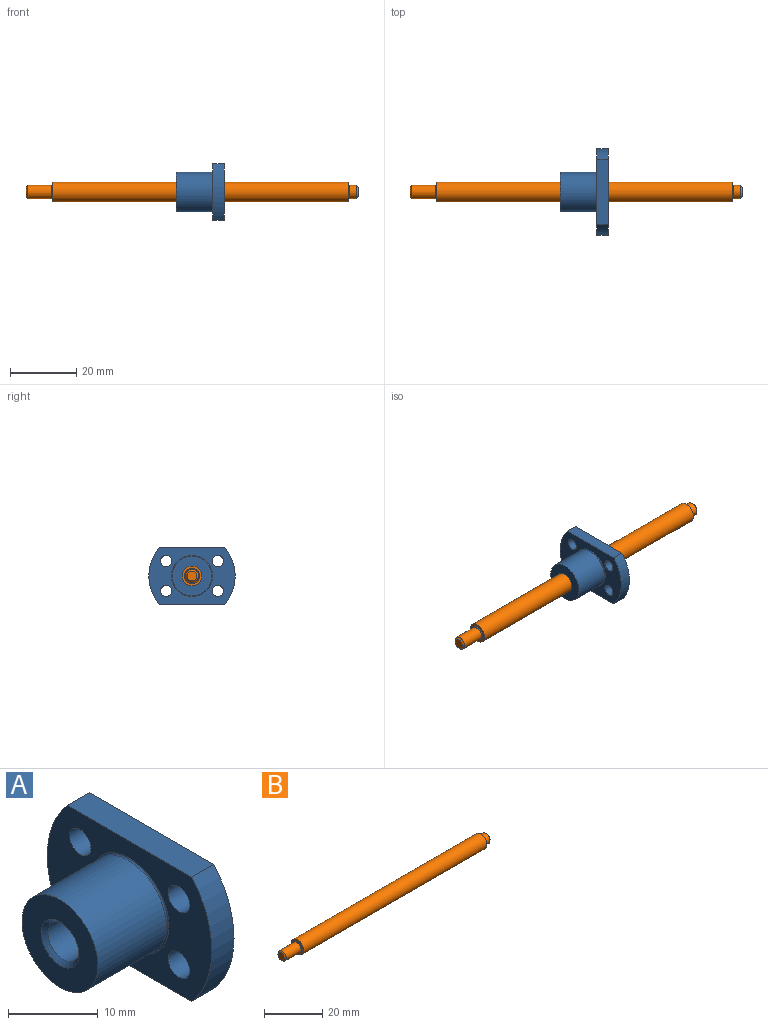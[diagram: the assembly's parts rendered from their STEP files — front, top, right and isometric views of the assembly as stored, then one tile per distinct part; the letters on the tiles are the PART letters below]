
ASSEMBLY  parts=2 mates=1
PART A: 16 faces, bbox 14.5x26x17 mm
  f0: plane 12x12mm, normal (-1,0,0), area 84.8mm2, adj f5,f7
  f1: plane 26x17mm, normal (1,0,0), area 343.5mm2, adj f2,f3,f6,f9,f10,f11,f12,f13
  f2: plane 19.67x3.5mm, normal (0,0,1), area 68.9mm2, adj f1,f3,f8,f14
  f3: cylinder r=13mm len=17mm, axis (1,0,0), area 64.9mm2, adj f1,f2,f8,f9
  f4: torus R=6.2mm, axis (1,0,0), area 12mm2, adj f5,f8
  f5: cylinder r=6mm len=12mm, axis (-1,0,0), area 407.2mm2, adj f0,f4
  f6: cone r=2.46mm half-angle=45deg, axis (1,0,0), area 13.1mm2, adj f1,f15
  f7: cone r=3mm half-angle=45deg, axis (-1,0,0), area 13.1mm2, adj f0,f15
  f8: plane 26x17mm, normal (-1,0,0), area 251mm2, adj f2,f3,f4,f9,f10,f11,f12,f13
  f9: plane 19.67x3.5mm, normal (0,0,-1), area 68.9mm2, adj f1,f3,f8,f14
  f10: cylinder r=1.7mm len=3.5mm, axis (1,0,0), area 37.4mm2, adj f1,f8
  f11: cylinder r=1.7mm len=3.5mm, axis (1,0,0), area 37.4mm2, adj f1,f8
  f12: cylinder r=1.7mm len=3.5mm, axis (1,0,0), area 37.4mm2, adj f1,f8
  f13: cylinder r=1.7mm len=3.5mm, axis (1,0,0), area 37.4mm2, adj f1,f8
  f14: cylinder r=13mm len=17mm, axis (1,0,0), area 64.9mm2, adj f1,f2,f8,f9
  f15: cylinder r=2.46mm len=13.42mm, axis (-1,0,0), area 207.3mm2, adj f6,f7
PART B: 11 faces, bbox 100x6x6 mm
  f0: plane 6x6mm, normal (1,0,0), area 11.7mm2, adj f5,f7
  f1: plane 6x6mm, normal (-1,0,0), area 11.7mm2, adj f6,f7
  f2: plane 3x3mm, normal (1,0,0), area 7.1mm2, adj f3
  f3: cone r=2mm half-angle=45deg, axis (-1,0,0), area 7.8mm2, adj f2,f4
  f4: cylinder r=2mm len=4mm, axis (-1,0,0), area 27.6mm2, adj f3,f5
  f5: torus R=2.3mm, axis (1,0,0), area 6.2mm2, adj f0,f4
  f6: torus R=2.3mm, axis (1,0,0), area 6.2mm2, adj f1,f10
  f7: cylinder r=3mm len=89mm, axis (-1,0,0), area 1677.6mm2, adj f0,f1
  f8: plane 3x3mm, normal (-1,0,0), area 7.1mm2, adj f9
  f9: cone r=1.5mm half-angle=45deg, axis (1,0,0), area 7.8mm2, adj f8,f10
  f10: cylinder r=2mm len=7.2mm, axis (-1,0,0), area 90.5mm2, adj f6,f9
PLACE A t=(45.25,0,0)mm
PLACE B at identity
MATE cylindrical B.f3 <-> A.f4  axis (-1,0,0) through (52.5,0,0)mm
